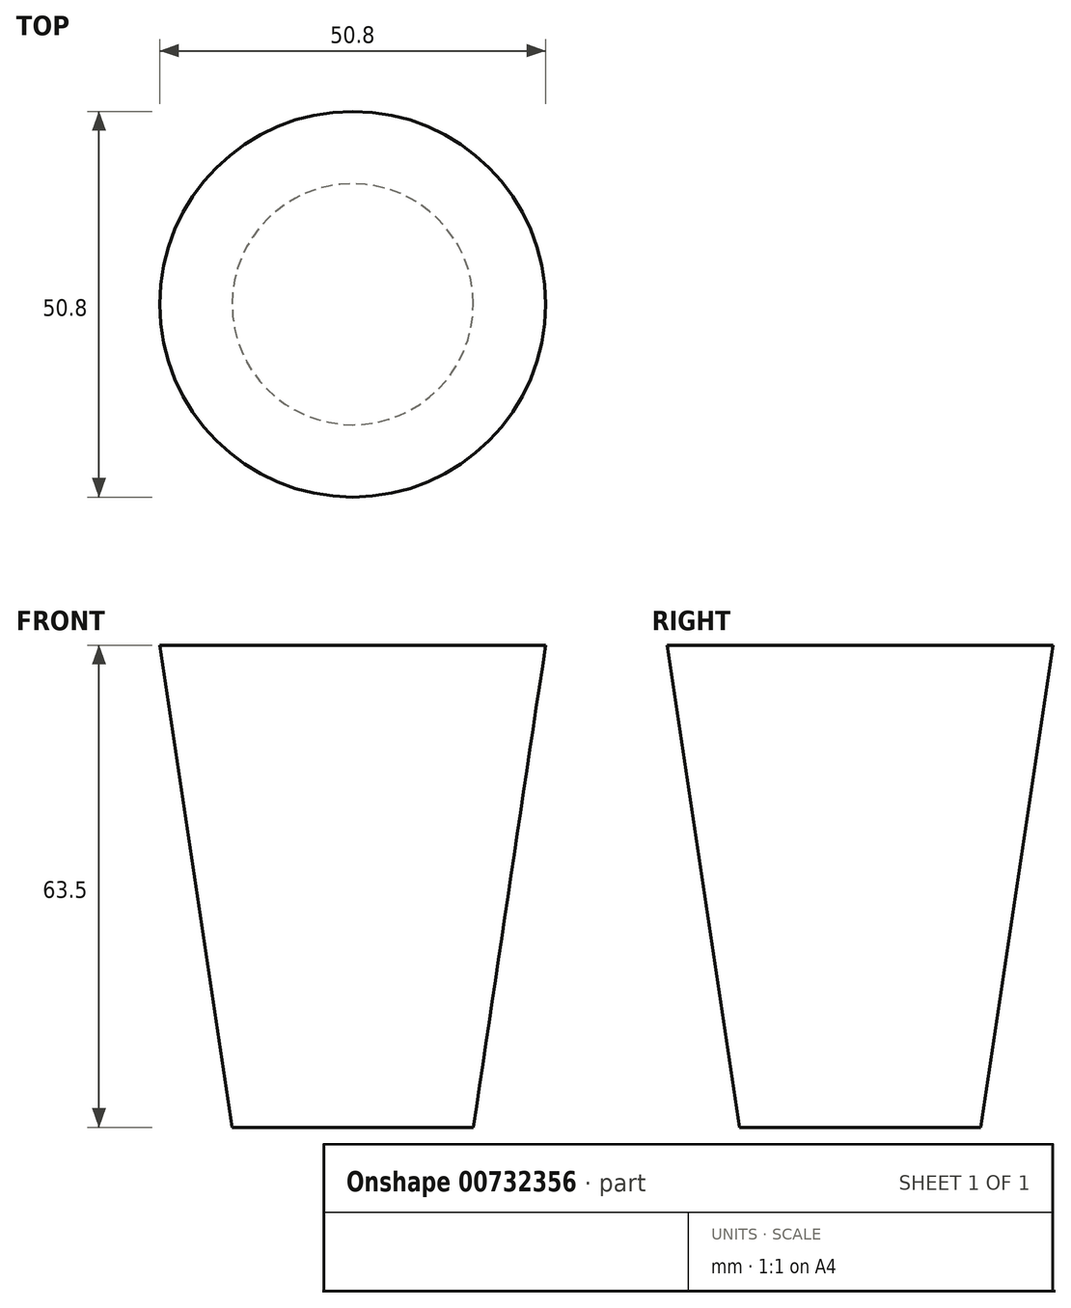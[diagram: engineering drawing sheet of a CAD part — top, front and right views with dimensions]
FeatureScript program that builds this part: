
annotation { "Feature Type Name" : "Feature", "Feature Type Description" : "" }
export const myFeature = defineFeature(function(context is Context, id is Id, definition is map)
    precondition{}
    {
        {
            var Q0;
            Q0=qCreatedBy(makeId("Top.planeOp"),FACE);
            var sketch = newSketch(context, id + "F0", { "sketchPlane" : qUnion([Q0])});
            skCircle(sketch, "E0", {"center": v(0, 0) * mm, "radius": 15.88 * mm});
            skSolve(sketch);
        }
        {
            var Q0;
            Q0=makeQuery(id+"F0.imprint","IMPRINT",FACE,{"disambiguationData":[TD([[makeQuery(id+"F0.imprint","IMPRINT",EDGE,{"derivedFrom":sQuery(id+"F0.wireOp",EDGE,"E0")}),1.0]])]});
            cPlane(context, id + "F1", {"entities" : qUnion([Q0]), "cplaneType" : CPlaneType.OFFSET, "offset" : 63.5 * mm, "width" : 152.4 * mm, "height" : 152.4 * mm});
        }
        {
            var Q0;
            Q0=qCreatedBy(id+"F1.planeOp",FACE);
            var sketch = newSketch(context, id + "F2", { "sketchPlane" : qUnion([Q0])});
            skCircle(sketch, "E1", {"center": v(0, 0) * mm, "radius": 25.4 * mm});
            skSolve(sketch);
        }
        {
            var Q0;
            Q0=makeQuery(id+"F2.imprint","IMPRINT",FACE,{"disambiguationData":[TD([[makeQuery(id+"F2.imprint","IMPRINT",EDGE,{"derivedFrom":sQuery(id+"F2.wireOp",EDGE,"E1")}),1.0]])]});
            var Q1;
            Q1=makeQuery(id+"F0.imprint","IMPRINT",FACE,{"disambiguationData":[TD([[makeQuery(id+"F0.imprint","IMPRINT",EDGE,{"derivedFrom":sQuery(id+"F0.wireOp",EDGE,"E0")}),1.0]])]});
            loft(context, id + "F3", {"sheetProfilesArray" : [{ "sheetProfileEntities" : qUnion([Q0]) }, { "sheetProfileEntities" : qUnion([Q1]) }]});
        }
    });
